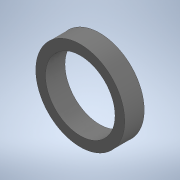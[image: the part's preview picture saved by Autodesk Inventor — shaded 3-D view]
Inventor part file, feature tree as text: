
AUTODESK INVENTOR PART (.ipt)
format: ipt  version: 2020 (Build 240168000, 168)  size: 101,888 bytes
history: native  units: mm
features: extrude x1, sketch x1
ambient origin geometry x8: Origin, YZ Plane, XZ Plane, XY Plane, X Axis, Y Axis, Z Axis, Center Point
bodies: Solid1 (feature_tree)
feature tree (2):
  extrude  "Extrusion1"  Depth=7.0mm
  sketch  "Sketch1"  dims[d0=32.0mm d1=25.0mm d2=7.0mm d3=0.0mm]
